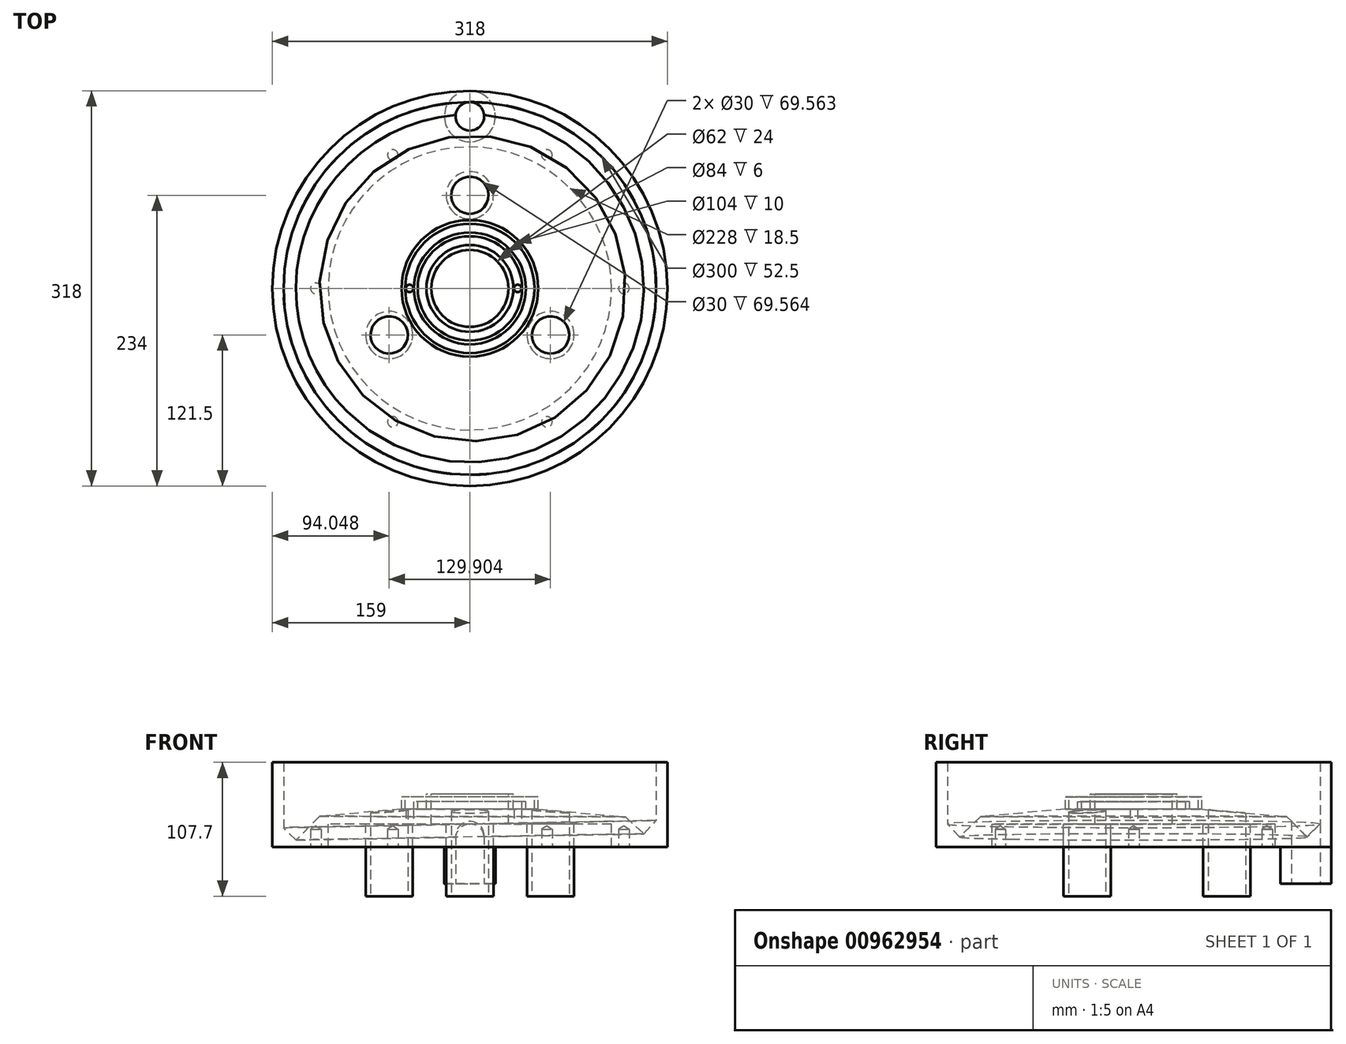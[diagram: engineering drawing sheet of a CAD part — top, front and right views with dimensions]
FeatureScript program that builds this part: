
annotation { "Feature Type Name" : "Feature", "Feature Type Description" : "" }
export const myFeature = defineFeature(function(context is Context, id is Id, definition is map)
    precondition{}
    {
        {
            var Q0;
            Q0=qCreatedBy(makeId("Front.planeOp"),FACE);
            var sketch = newSketch(context, id + "F0", { "sketchPlane" : qUnion([Q0])});
            skLineSegment(sketch, "E0", {"start": v(0, 128.6) * mm, "end": v(0, -171.4) * mm, "construction": true});
            skLineSegment(sketch, "E1", {"start": v(-31, 42.5) * mm, "end": v(-35, 42.5) * mm});
            skLineSegment(sketch, "E2", {"start": v(-35, 42.5) * mm, "end": v(-35, 30.5) * mm});
            skLineSegment(sketch, "E3", {"start": v(-35, 30.5) * mm, "end": v(-42, 30.5) * mm});
            skLineSegment(sketch, "E4", {"start": v(-42, 30.5) * mm, "end": v(-42, 36.5) * mm});
            skLineSegment(sketch, "E5", {"start": v(-42, 36.5) * mm, "end": v(-45, 36.5) * mm});
            skLineSegment(sketch, "E6", {"start": v(-45, 36.5) * mm, "end": v(-45, 30.5) * mm});
            skLineSegment(sketch, "E7", {"start": v(-45, 30.5) * mm, "end": v(-52, 30.5) * mm});
            skLineSegment(sketch, "E8", {"start": v(-52, 30.5) * mm, "end": v(-52, 40.5) * mm});
            skLineSegment(sketch, "E9", {"start": v(-52, 40.5) * mm, "end": v(-55, 40.5) * mm});
            skLineSegment(sketch, "E10", {"start": v(-55, 40.5) * mm, "end": v(-55, 30.5) * mm});
            skLineSegment(sketch, "E11", {"start": v(-55, 30.5) * mm, "end": v(-159, 21.4) * mm});
            skLineSegment(sketch, "E12", {"start": v(-31, 42.5) * mm, "end": v(-31, 18.5) * mm});
            skLineSegment(sketch, "E13", {"start": v(-31, 18.5) * mm, "end": v(-114, 18.5) * mm});
            skLineSegment(sketch, "E14", {"start": v(-114, 18.5) * mm, "end": v(-114, 0) * mm});
            skLineSegment(sketch, "E15", {"start": v(-114, 0) * mm, "end": v(-159, 0) * mm});
            skLineSegment(sketch, "E16", {"start": v(-159, 0) * mm, "end": v(-159, 21.4) * mm});
            skSolve(sketch);
        }
        {
            var Q0;
            Q0 = qSketchRegion(id + "F0", true);
            var Q1;
            Q1=sQuery(id+"F0.wireOp",EDGE,"E0");
            revolve(context, id + "F1", {"surfaceOperationType" : NewSurfaceOperationType.NEW, "entities" : qUnion([Q0]), "axis" : qUnion([Q1]), "revolveType" : RevolveType.FULL});
        }
        {
            var Q0;
            Q0=qCreatedBy(makeId("Front.planeOp"),FACE);
            var sketch = newSketch(context, id + "F2", { "sketchPlane" : qUnion([Q0])});
            skLineSegment(sketch, "E17", {"start": v(0, 25.46) * mm, "end": v(0, -24.58) * mm, "construction": true});
            skLineSegment(sketch, "E18", {"start": v(-140, 5.7) * mm, "end": v(140, 10.7) * mm, "construction": true});
            skLineSegment(sketch, "E19", {"start": v(-0.88, 57.64) * mm, "end": v(0, 8.2) * mm, "construction": true});
            skLineSegment(sketch, "E20", {"start": v(-140, 5.7) * mm, "end": v(-164.23, 29.93) * mm});
            skLineSegment(sketch, "E21", {"start": v(-140, 5.7) * mm, "end": v(-111.17, 34.53) * mm});
            skLineSegment(sketch, "E22", {"start": v(-140, 35.35) * mm, "end": v(-140, -15.61) * mm, "construction": true});
            skLineSegment(sketch, "E23", {"start": v(-164.23, 29.93) * mm, "end": v(-111.17, 34.53) * mm});
            skSolve(sketch);
        }
        {
            var Q0;
            Q0 = qSketchRegion(id + "F2", true);
            var Q1;
            Q1=sQuery(id+"F2.wireOp",EDGE,"E19");
            revolve(context, id + "F3", {"operationType" : NewBodyOperationType.REMOVE, "surfaceOperationType" : NewSurfaceOperationType.NEW, "entities" : qUnion([Q0]), "axis" : qUnion([Q1]), "revolveType" : RevolveType.FULL, "oppositeDirection" : true});
        }
        {
            var Q0;
            Q0=makeQuery(id+"F1.opRevolve","SWEPT_FACE",FACE,{"disambiguationData":[OSD([sQuery(id+"F0.wireOp",EDGE,"E15")])]});
            var sketch = newSketch(context, id + "F4", { "sketchPlane" : qUnion([Q0])});
            skCircle(sketch, "E24", {"center": v(0, 0) * mm, "radius": 150 * mm});
            skCircle(sketch, "E25", {"center": v(0, 0) * mm, "radius": 159 * mm});
            skSolve(sketch);
        }
        {
            var Q0;
            Q0 = qSketchRegion(id + "F4", true);
            extrude(context, id + "F5", {"entities" : qUnion([Q0]), "operationType" : NewBodyOperationType.ADD, "oppositeDirection" : true, "depth" : 68.2 * mm, "offsetDistance" : 25 * mm});
        }
        {
            var Q0;
            Q0=makeQuery(id+"F1.opRevolve","SWEPT_FACE",FACE,{"disambiguationData":[OSD([sQuery(id+"F0.wireOp",EDGE,"E13")])]});
            var sketch = newSketch(context, id + "F6", { "sketchPlane" : qUnion([Q0])});
            skPoint(sketch, "E26", {"position": v(-48.5, 0) * mm});
            skPoint(sketch, "E27", {"position": v(38.5, 0) * mm});
            skSolve(sketch);
        }
        {
            var Q0;
            Q0=sQuery(id+"F6.wireOp",VERTEX,"E26");
            var Q1;
            Q1=sQuery(id+"F6.wireOp",VERTEX,"E27");
            var Q2;
            Q2=makeQuery(id+"F1.opRevolve","SWEPT_BODY",BODY,{"disambiguationData":[OSD([sQuery(id+"F0.wireOp",EDGE,"E1"),sQuery(id+"F0.wireOp",EDGE,"E2"),sQuery(id+"F0.wireOp",EDGE,"E3"),sQuery(id+"F0.wireOp",EDGE,"E4"),sQuery(id+"F0.wireOp",EDGE,"E5"),sQuery(id+"F0.wireOp",EDGE,"E6"),sQuery(id+"F0.wireOp",EDGE,"E7"),sQuery(id+"F0.wireOp",EDGE,"E8"),sQuery(id+"F0.wireOp",EDGE,"E9"),sQuery(id+"F0.wireOp",EDGE,"E10"),sQuery(id+"F0.wireOp",EDGE,"E11"),sQuery(id+"F0.wireOp",EDGE,"E12"),sQuery(id+"F0.wireOp",EDGE,"E13"),sQuery(id+"F0.wireOp",EDGE,"E14"),sQuery(id+"F0.wireOp",EDGE,"E15"),sQuery(id+"F0.wireOp",EDGE,"E16")])]});
            hole(context, id + "F7", {"style" : HoleStyle.SIMPLE, "endStyle" : HoleEndStyle.THROUGH, "standardTappedOrClearance" : lookupTablePath({ "standard" : "ISO", "size" : "6", "type" : "Drilled" }), "standardBlindInLast" : lookupTablePath({ "standard" : "ISO", "size" : "6", "type" : "Drilled" }), "holeDiameter" : 6 * mm, "majorDiameter" : 5 * mm, "isTappedThrough" : true, "tappedDepth" : 12 * mm, "tapClearance" : 3, "locations" : qUnion([Q0, Q1]), "scope" : qUnion([Q2])});
        }
        {
            var Q0;
            Q0=makeQuery(id+"F1.opRevolve","SWEPT_FACE",FACE,{"disambiguationData":[OSD([sQuery(id+"F0.wireOp",EDGE,"E15")])]});
            var sketch = newSketch(context, id + "F8", { "sketchPlane" : qUnion([Q0])});
            skPoint(sketch, "E28", {"position": v(-124, 0) * mm});
            skPoint(sketch, "E29.1.0", {"position": v(-62, -107.39) * mm});
            skPoint(sketch, "E29.2.0", {"position": v(62, -107.39) * mm});
            skPoint(sketch, "E29.3.0", {"position": v(124, 0) * mm});
            skPoint(sketch, "E29.4.0", {"position": v(62, 107.39) * mm});
            skPoint(sketch, "E29.5.0", {"position": v(-62, 107.39) * mm});
            skPoint(sketch, "E29.center", {"position": v(0, 0) * mm});
            skSolve(sketch);
        }
        {
            var Q0;
            Q0=sQuery(id+"F8.wireOp",VERTEX,"E29.5.0");
            var Q1;
            Q1=sQuery(id+"F8.wireOp",VERTEX,"E28");
            var Q2;
            Q2=sQuery(id+"F8.wireOp",VERTEX,"E29.1.0");
            var Q3;
            Q3=sQuery(id+"F8.wireOp",VERTEX,"E29.2.0");
            var Q4;
            Q4=sQuery(id+"F8.wireOp",VERTEX,"E29.3.0");
            var Q5;
            Q5=sQuery(id+"F8.wireOp",VERTEX,"E29.4.0");
            var Q6;
            Q6=makeQuery(id+"F1.opRevolve","SWEPT_BODY",BODY,{"disambiguationData":[OSD([sQuery(id+"F0.wireOp",EDGE,"E1"),sQuery(id+"F0.wireOp",EDGE,"E2"),sQuery(id+"F0.wireOp",EDGE,"E3"),sQuery(id+"F0.wireOp",EDGE,"E4"),sQuery(id+"F0.wireOp",EDGE,"E5"),sQuery(id+"F0.wireOp",EDGE,"E6"),sQuery(id+"F0.wireOp",EDGE,"E7"),sQuery(id+"F0.wireOp",EDGE,"E8"),sQuery(id+"F0.wireOp",EDGE,"E9"),sQuery(id+"F0.wireOp",EDGE,"E10"),sQuery(id+"F0.wireOp",EDGE,"E11"),sQuery(id+"F0.wireOp",EDGE,"E12"),sQuery(id+"F0.wireOp",EDGE,"E13"),sQuery(id+"F0.wireOp",EDGE,"E14"),sQuery(id+"F0.wireOp",EDGE,"E15"),sQuery(id+"F0.wireOp",EDGE,"E16")])]});
            hole(context, id + "F9", {"style" : HoleStyle.SIMPLE, "endStyle" : HoleEndStyle.BLIND, "standardTappedOrClearance" : lookupTablePath({ "standard" : "ISO", "engagement" : "75%", "pitch" : "1.5 mm", "size" : "M10", "type" : "Tapped" }), "standardBlindInLast" : lookupTablePath({ "standard" : "ISO", "fit" : "Normal", "engagement" : "75%", "pitch" : "1.5 mm", "size" : "M10", "type" : "Clearance & tapped" }), "holeDiameter" : 8.5 * mm, "majorDiameter" : 10 * mm, "showTappedDepth" : true, "holeDepth" : 14.5 * mm, "isTappedThrough" : true, "tappedDepth" : 10 * mm, "tapClearance" : 3, "startFromSketch" : true, "locations" : qUnion([Q0, Q1, Q2, Q3, Q4, Q5]), "scope" : qUnion([Q6])});
        }
        {
            var Q0;
            Q0=makeQuery(id+"F1.opRevolve","SWEPT_FACE",FACE,{"disambiguationData":[OSD([sQuery(id+"F0.wireOp",EDGE,"E13")])]});
            var sketch = newSketch(context, id + "F10", { "sketchPlane" : qUnion([Q0])});
            skCircle(sketch, "E30", {"center": v(0, -75) * mm, "radius": 19 * mm});
            skCircle(sketch, "E31.1.0", {"center": v(64.95, 37.5) * mm, "radius": 19 * mm});
            skCircle(sketch, "E31.2.0", {"center": v(-64.95, 37.5) * mm, "radius": 19 * mm});
            skPoint(sketch, "E31.center", {"position": v(0, 0) * mm});
            skSolve(sketch);
        }
        {
            var Q0;
            Q0=makeQuery(id+"F10.imprint","IMPRINT",FACE,{"disambiguationData":[TD([[makeQuery(id+"F10.imprint","IMPRINT",EDGE,{"derivedFrom":sQuery(id+"F10.wireOp",EDGE,"E31.2.0")}),1.0]])]});
            var Q1;
            Q1=makeQuery(id+"F10.imprint","IMPRINT",FACE,{"disambiguationData":[TD([[makeQuery(id+"F10.imprint","IMPRINT",EDGE,{"derivedFrom":sQuery(id+"F10.wireOp",EDGE,"E30")}),1.0]])]});
            var Q2;
            Q2=makeQuery(id+"F10.imprint","IMPRINT",FACE,{"disambiguationData":[TD([[makeQuery(id+"F10.imprint","IMPRINT",EDGE,{"derivedFrom":sQuery(id+"F10.wireOp",EDGE,"E31.1.0")}),1.0]])]});
            extrude(context, id + "F11", {"entities" : qUnion([Q0, Q1, Q2]), "operationType" : NewBodyOperationType.ADD, "depth" : 58 * mm, "offsetDistance" : 25 * mm});
        }
        {
            var Q0;
            Q0=makeQuery(id+"F11.opExtrude","CAP_FACE",FACE,{"disambiguationData":[OSD([sQuery(id+"F10.wireOp",EDGE,"E31.2.0")])],"isStart":false});
            var sketch = newSketch(context, id + "F12", { "sketchPlane" : qUnion([Q0])});
            skCircle(sketch, "E32", {"center": v(-64.95, 37.5) * mm, "radius": 15 * mm});
            skCircle(sketch, "E33.1.0", {"center": v(0, -75) * mm, "radius": 15 * mm});
            skCircle(sketch, "E33.2.0", {"center": v(64.95, 37.5) * mm, "radius": 15 * mm});
            skPoint(sketch, "E33.center", {"position": v(0, 0) * mm});
            skSolve(sketch);
        }
        {
            var Q0;
            Q0=makeQuery(id+"F12.imprint","IMPRINT",FACE,{"disambiguationData":[TD([[makeQuery(id+"F12.imprint","IMPRINT",EDGE,{"derivedFrom":sQuery(id+"F12.wireOp",EDGE,"E32")}),1.0]])]});
            var Q1;
            Q1=makeQuery(id+"F12.imprint","IMPRINT",FACE,{"disambiguationData":[TD([[makeQuery(id+"F12.imprint","IMPRINT",EDGE,{"derivedFrom":sQuery(id+"F12.wireOp",EDGE,"E33.2.0")}),1.0]])]});
            var Q2;
            Q2=makeQuery(id+"F12.imprint","IMPRINT",FACE,{"disambiguationData":[TD([[makeQuery(id+"F12.imprint","IMPRINT",EDGE,{"derivedFrom":sQuery(id+"F12.wireOp",EDGE,"E33.1.0")}),1.0]])]});
            extrude(context, id + "F13", {"entities" : qUnion([Q0, Q1, Q2]), "operationType" : NewBodyOperationType.REMOVE, "endBound" : BoundingType.UP_TO_NEXT, "oppositeDirection" : true, "depth" : 25 * mm, "offsetDistance" : 25 * mm});
        }
        {
            var Q0;
            Q0=makeQuery(id+"F1.opRevolve","SWEPT_FACE",FACE,{"disambiguationData":[OSD([sQuery(id+"F0.wireOp",EDGE,"E15")])]});
            var sketch = newSketch(context, id + "F14", { "sketchPlane" : qUnion([Q0])});
            skCircle(sketch, "E34", {"center": v(0, -138.5) * mm, "radius": 20.5 * mm});
            skSolve(sketch);
        }
        {
            var Q0;
            Q0 = qSketchRegion(id + "F14", true);
            extrude(context, id + "F15", {"entities" : qUnion([Q0]), "operationType" : NewBodyOperationType.ADD, "depth" : 29.5 * mm, "offsetDistance" : 25 * mm});
        }
        {
            var Q0;
            Q0=makeQuery(id+"F15.opExtrude","CAP_FACE",FACE,{"disambiguationData":[OSD([sQuery(id+"F14.wireOp",EDGE,"E34")])],"isStart":false});
            var sketch = newSketch(context, id + "F16", { "sketchPlane" : qUnion([Q0])});
            skCircle(sketch, "E35", {"center": v(0, -138.5) * mm, "radius": 11.5 * mm});
            skSolve(sketch);
        }
        {
            var Q0;
            Q0 = qSketchRegion(id + "F16", true);
            extrude(context, id + "F17", {"entities" : qUnion([Q0]), "operationType" : NewBodyOperationType.REMOVE, "endBound" : BoundingType.UP_TO_NEXT, "oppositeDirection" : true, "depth" : 25 * mm, "offsetDistance" : 25 * mm});
        }
    });
